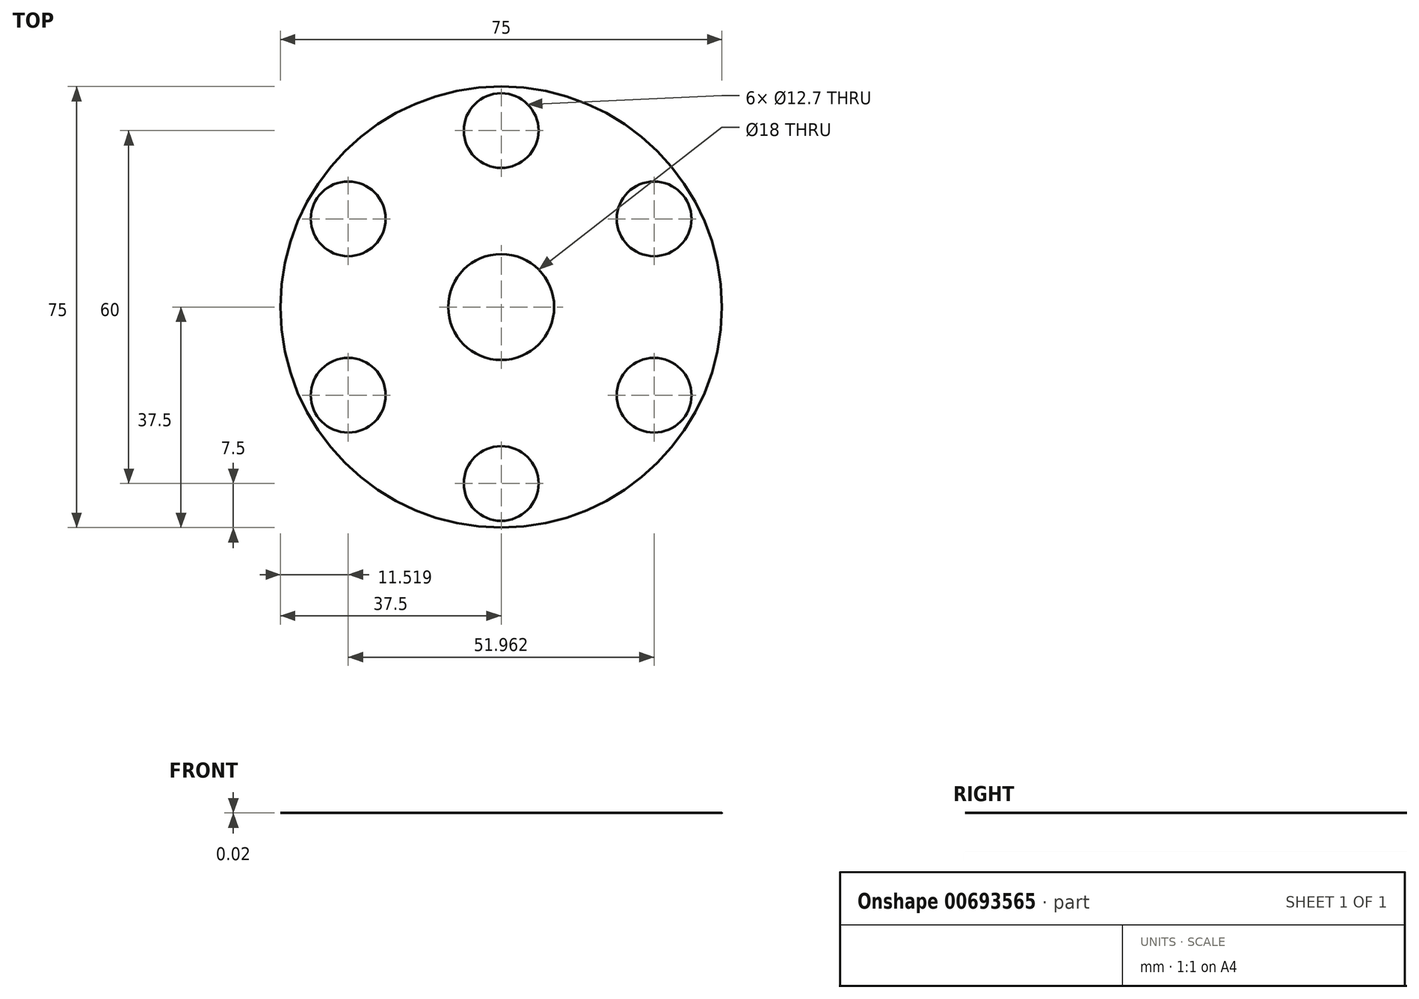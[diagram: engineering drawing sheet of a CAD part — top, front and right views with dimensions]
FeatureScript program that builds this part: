
annotation { "Feature Type Name" : "Feature", "Feature Type Description" : "" }
export const myFeature = defineFeature(function(context is Context, id is Id, definition is map)
    precondition{}
    {
        {
            var Q0;
            Q0=qCreatedBy(makeId("Top.planeOp"),FACE);
            var sketch = newSketch(context, id + "F0", { "sketchPlane" : qUnion([Q0])});
            skCircle(sketch, "E0", {"center": v(0, 0) * mm, "radius": 37.5 * mm});
            skSolve(sketch);
        }
        {
            var Q0;
            Q0 = qSketchRegion(id + "F0", true);
            extrude(context, id + "F1", {"entities" : qUnion([Q0]), "depth" : 1 / 50.8 * mm, "offsetDistance" : 25 * mm});
        }
        {
            var Q0;
            Q0=makeQuery(id+"F1.opExtrude","CAP_FACE",FACE,{"disambiguationData":[OSD([sQuery(id+"F0.wireOp",EDGE,"E0")])],"isStart":false});
            var sketch = newSketch(context, id + "F2", { "sketchPlane" : qUnion([Q0])});
            skPoint(sketch, "E1", {"position": v(0, 0) * mm});
            skSolve(sketch);
        }
        {
            var Q0;
            Q0=sQuery(id+"F2.wireOp",VERTEX,"E1");
            var Q1;
            Q1=makeQuery(id+"F1.opExtrude","SWEPT_BODY",BODY,{"disambiguationData":[OSD([sQuery(id+"F0.wireOp",EDGE,"E0")])]});
            hole(context, id + "F3", {"style" : HoleStyle.SIMPLE, "endStyle" : HoleEndStyle.THROUGH, "holeDiameter" : 18 * mm, "majorDiameter" : 5 * mm, "isTappedThrough" : true, "tappedDepth" : 12 * mm, "tapClearance" : 3, "startFromSketch" : true, "locations" : qUnion([Q0]), "scope" : qUnion([Q1])});
        }
        {
            var Q0;
            Q0=makeQuery(id+"F1.opExtrude","CAP_FACE",FACE,{"disambiguationData":[OSD([sQuery(id+"F0.wireOp",EDGE,"E0")])],"isStart":false});
            var sketch = newSketch(context, id + "F4", { "sketchPlane" : qUnion([Q0])});
            skCircle(sketch, "E2.cCircle", {"center": v(0, 0) * mm, "radius": 25.98 * mm, "construction": true});
            skLineSegment(sketch, "E2.0", {"start": v(25.98, -15) * mm, "end": v(0, -30) * mm, "construction": true});
            skLineSegment(sketch, "E2.1", {"start": v(0, -30) * mm, "end": v(-25.98, -15) * mm, "construction": true});
            skLineSegment(sketch, "E2.2", {"start": v(-25.98, -15) * mm, "end": v(-25.98, 15) * mm, "construction": true});
            skLineSegment(sketch, "E2.3", {"start": v(-25.98, 15) * mm, "end": v(0, 30) * mm, "construction": true});
            skLineSegment(sketch, "E2.4", {"start": v(0, 30) * mm, "end": v(25.98, 15) * mm, "construction": true});
            skLineSegment(sketch, "E2.5", {"start": v(25.98, 15) * mm, "end": v(25.98, -15) * mm, "construction": true});
            skPoint(sketch, "E2.0.midPoint", {"position": v(13, -22.5) * mm});
            skSolve(sketch);
        }
        {
            var Q0;
            Q0=sQuery(id+"F4.wireOp",VERTEX,"E2.4.start");
            var Q1;
            Q1=sQuery(id+"F4.wireOp",VERTEX,"E2.5.start");
            var Q2;
            Q2=sQuery(id+"F4.wireOp",VERTEX,"E2.5.end");
            var Q3;
            Q3=sQuery(id+"F4.wireOp",VERTEX,"E2.0.end");
            var Q4;
            Q4=sQuery(id+"F4.wireOp",VERTEX,"E2.2.start");
            var Q5;
            Q5=sQuery(id+"F4.wireOp",VERTEX,"E2.3.start");
            var Q6;
            Q6=makeQuery(id+"F1.opExtrude","SWEPT_BODY",BODY,{"disambiguationData":[OSD([sQuery(id+"F0.wireOp",EDGE,"E0")])]});
            hole(context, id + "F5", {"style" : HoleStyle.C_BORE, "endStyle" : HoleEndStyle.THROUGH, "holeDiameter" : 6.5 * mm, "cBoreDiameter" : 12.7 * mm, "cBoreDepth" : 10 * mm, "majorDiameter" : 5 * mm, "isTappedThrough" : true, "tappedDepth" : 12 * mm, "tapClearance" : 3, "startFromSketch" : true, "locations" : qUnion([Q0, Q1, Q2, Q3, Q4, Q5]), "scope" : qUnion([Q6])});
        }
    });
